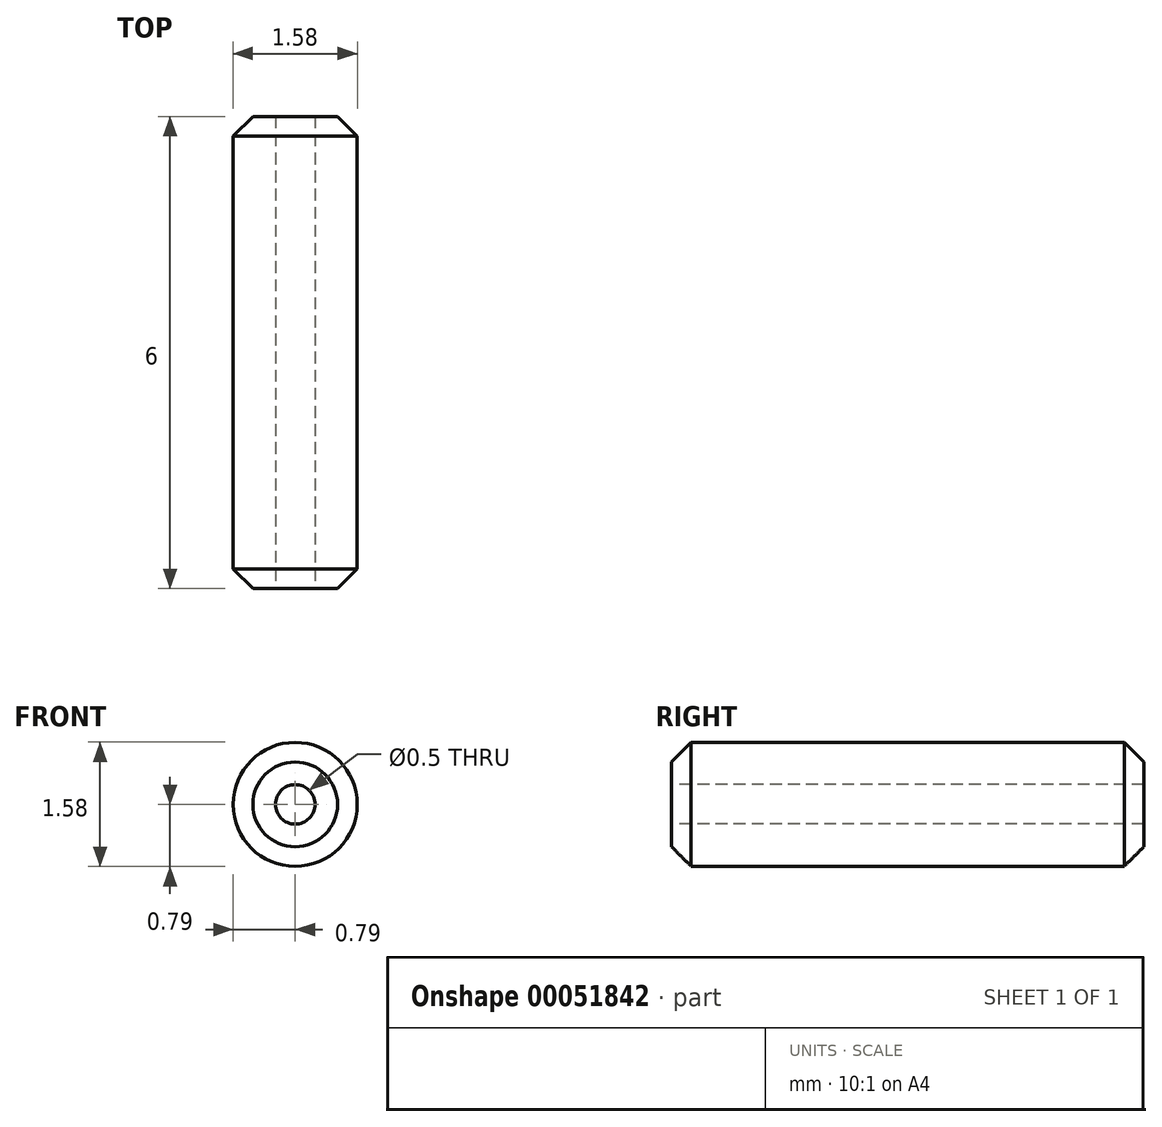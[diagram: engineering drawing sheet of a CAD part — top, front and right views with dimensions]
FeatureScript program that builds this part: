
annotation { "Feature Type Name" : "Feature", "Feature Type Description" : "" }
export const myFeature = defineFeature(function(context is Context, id is Id, definition is map)
    precondition{}
    {
        {
            var Q0;
            Q0=qCreatedBy(makeId("Right.planeOp"),FACE);
            var sketch = newSketch(context, id + "F0", { "sketchPlane" : qUnion([Q0])});
            skLineSegment(sketch, "E0.top", {"start": v(0, 0.79) * mm, "end": v(6, 0.79) * mm});
            skLineSegment(sketch, "E0.left", {"start": v(0, 0.25) * mm, "end": v(0, 0.79) * mm});
            skLineSegment(sketch, "E0.right", {"start": v(6, 0.25) * mm, "end": v(6, 0.79) * mm});
            skLineSegment(sketch, "E1.top", {"start": v(0, 0.25) * mm, "end": v(6, 0.25) * mm});
            skLineSegment(sketch, "E1.left", {"start": v(0, 0.79) * mm, "end": v(0, 0.25) * mm});
            skLineSegment(sketch, "E1.right", {"start": v(6, 0.79) * mm, "end": v(6, 0.25) * mm});
            skLineSegment(sketch, "E2", {"start": v(0, 0) * mm, "end": v(6, 0) * mm, "construction": true});
            skSolve(sketch);
        }
        {
            var Q0;
            Q0 = qSketchRegion(id + "F0", true);
            var Q1;
            Q1=sQuery(id+"F0.wireOp",EDGE,"E2");
            revolve(context, id + "F1", {"entities" : qUnion([Q0]), "axis" : qUnion([Q1]), "revolveType" : RevolveType.FULL});
        }
        {
            var Q0;
            Q0=makeQuery(id+"F1.opRevolve","SWEPT_EDGE",EDGE,{"disambiguationData":[OSD([sQuery(id+"F0.wireOp",EDGE,"E0.top"),sQuery(id+"F0.wireOp",EDGE,"E1.left")])]});
            var Q1;
            Q1=makeQuery(id+"F1.opRevolve","SWEPT_EDGE",EDGE,{"disambiguationData":[OSD([sQuery(id+"F0.wireOp",EDGE,"E0.top"),sQuery(id+"F0.wireOp",EDGE,"E1.right")])]});
            chamfer(context, id + "F2", {"entities" : qUnion([Q0, Q1]), "width" : 0.25 * mm, "tangentPropagation" : true});
        }
    });
